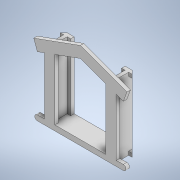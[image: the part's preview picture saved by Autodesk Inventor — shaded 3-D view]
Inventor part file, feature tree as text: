
AUTODESK INVENTOR PART (.ipt)
format: ipt  version: 2021 (Build 250183000, 183)  size: 208,384 bytes
history: native  units: mm
features: extrude x5, sketch x5, projected_geometry x4
ambient origin geometry x8: Origin, YZ Plane, XZ Plane, XY Plane, X Axis, Y Axis, Z Axis, Center Point
bodies: Volumenkörper1 (feature_tree)
feature tree (14):
  extrude  "Extrusion1"  Depth=20.5mm
  extrude  "Extrusion2"  Depth=3.5mm
  extrude  "Extrusion3"  Depth=19.0mm TaperAngle=0.0deg
  extrude  "Extrusion4"  Depth=2.0mm
  extrude  "Extrusion5"  Depth=1.0mm
  sketch  "Skizze1"  dims[d0=18.5mm d1=20.5mm]
  sketch  "Skizze2"  dims[d2=5.5mm d3=0.0mm d4=3.5mm]
  projected_geometry  "Projizierte Kontur1"
  sketch  "Skizze3"  dims[d5=1.0mm d6=19.0mm d7=0.0mm]
  projected_geometry  "Projizierte Kontur2"
  sketch  "Skizze4"  dims[d8=2.0mm d9=2.0mm]
  projected_geometry  "Projizierte Kontur3"
  sketch  "Skizze5"  dims[d10=1.0mm d11=1.0mm d12=19.0mm d13=0.0mm d14=1.0mm d15=0.0mm d16=0.0mm d18=3.0mm d19=1.0mm d20=0.0mm d21=1.0mm d22=0.0mm d31=3.490659mm d32=3.0mm d33=1.0mm]
  projected_geometry  "Projizierte Kontur4"
